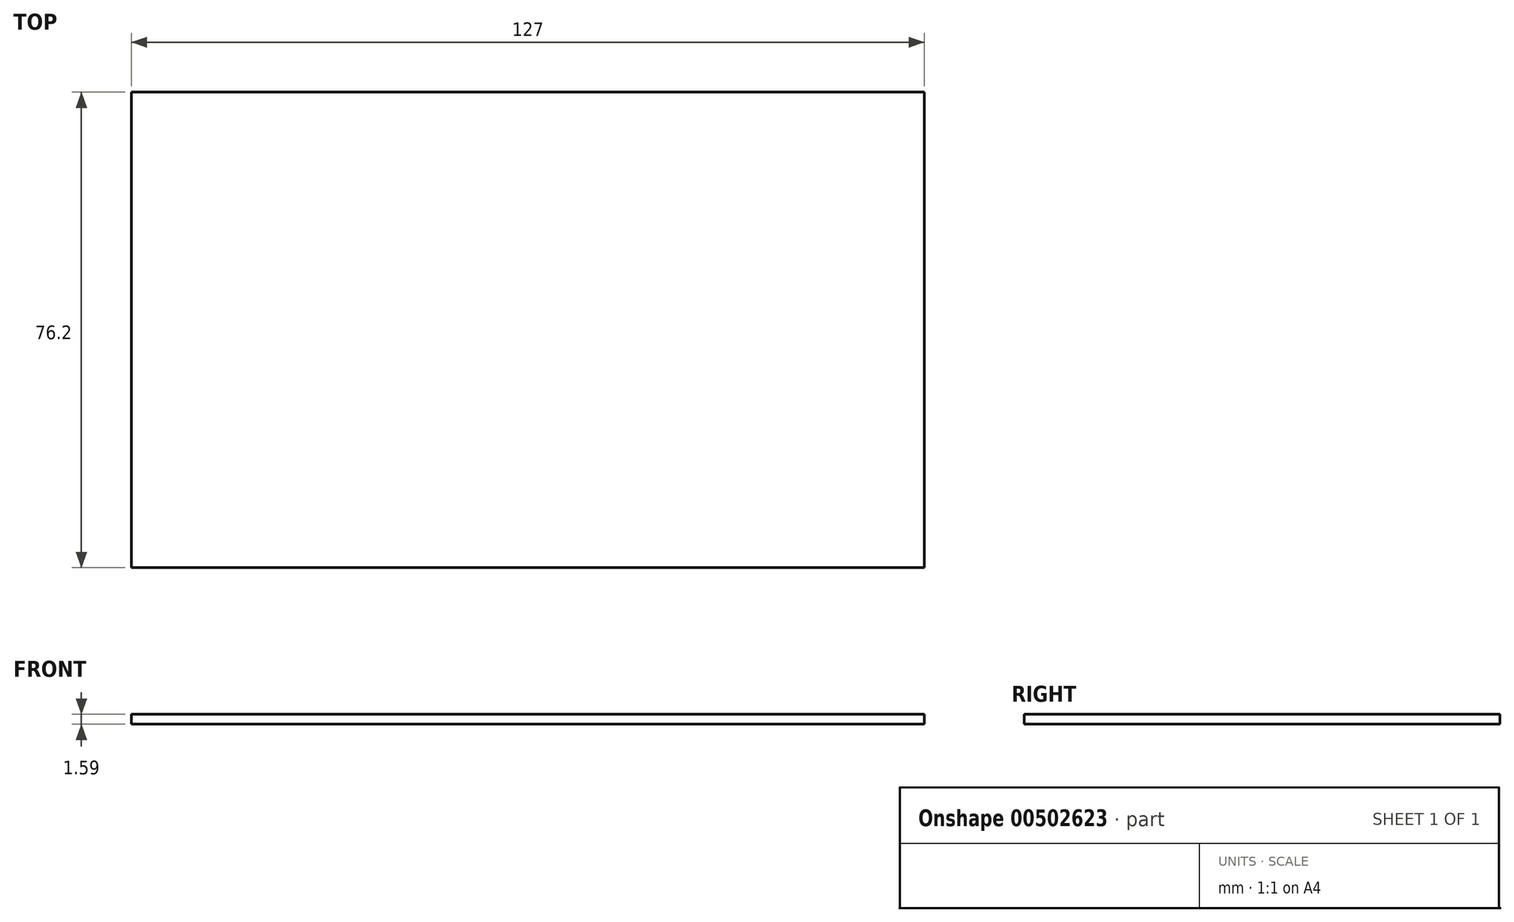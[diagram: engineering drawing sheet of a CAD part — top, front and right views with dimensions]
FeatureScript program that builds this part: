
annotation { "Feature Type Name" : "Feature", "Feature Type Description" : "" }
export const myFeature = defineFeature(function(context is Context, id is Id, definition is map)
    precondition{}
    {
        {
            var Q0;
            Q0=qCreatedBy(makeId("Top.planeOp"),FACE);
            var sketch = newSketch(context, id + "F0", { "sketchPlane" : qUnion([Q0])});
            skLineSegment(sketch, "E0.bottom", {"start": v(0, 0) * mm, "end": v(127, 0) * mm});
            skLineSegment(sketch, "E0.top", {"start": v(0, 76.2) * mm, "end": v(127, 76.2) * mm});
            skLineSegment(sketch, "E0.left", {"start": v(0, 0) * mm, "end": v(0, 76.2) * mm});
            skLineSegment(sketch, "E0.right", {"start": v(127, 0) * mm, "end": v(127, 76.2) * mm});
            skSolve(sketch);
        }
        {
            var Q0;
            Q0=makeQuery(id+"F0.imprint","IMPRINT",FACE,{"disambiguationData":[TD([[makeQuery(id+"F0.imprint","IMPRINT",EDGE,{"derivedFrom":sQuery(id+"F0.wireOp",EDGE,"E0.bottom")}),1.0]])]});
            extrude(context, id + "F1", {"entities" : qUnion([Q0]), "depth" : 1.59 * mm});
        }
    });
